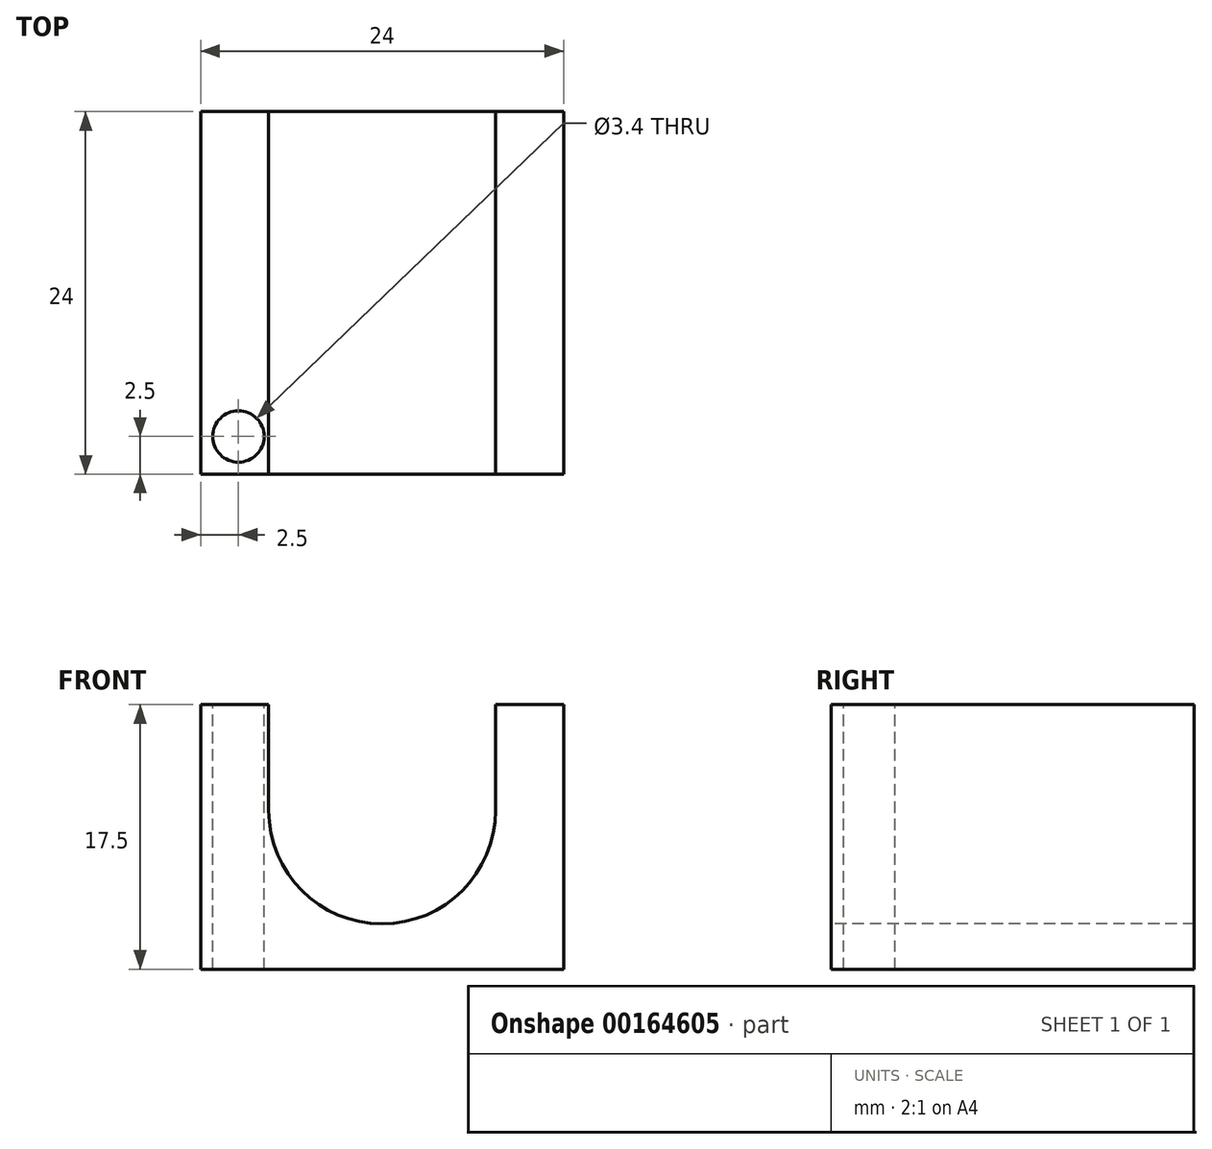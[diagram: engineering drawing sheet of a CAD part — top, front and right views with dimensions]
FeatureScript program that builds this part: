
annotation { "Feature Type Name" : "Feature", "Feature Type Description" : "" }
export const myFeature = defineFeature(function(context is Context, id is Id, definition is map)
    precondition{}
    {
        {
            var Q0;
            Q0=qCreatedBy(makeId("Top.planeOp"),FACE);
            var sketch = newSketch(context, id + "F0", { "sketchPlane" : qUnion([Q0])});
            skLineSegment(sketch, "E0.bottom", {"start": v(12, 12) * mm, "end": v(-12, 12) * mm});
            skLineSegment(sketch, "E0.top", {"start": v(12, -12) * mm, "end": v(-12, -12) * mm});
            skLineSegment(sketch, "E0.left", {"start": v(12, 12) * mm, "end": v(12, -12) * mm});
            skLineSegment(sketch, "E0.right", {"start": v(-12, 12) * mm, "end": v(-12, -12) * mm});
            skPoint(sketch, "E0.middle", {"position": v(0, 0) * mm});
            skSolve(sketch);
        }
        {
            var Q0;
            Q0=makeQuery(id+"F0.imprint","IMPRINT",FACE,{"disambiguationData":[TD([[makeQuery(id+"F0.imprint","IMPRINT",EDGE,{"derivedFrom":sQuery(id+"F0.wireOp",EDGE,"E0.bottom")}),1.0]])]});
            extrude(context, id + "F1", {"entities" : qUnion([Q0]), "depth" : 17.5 * mm});
        }
        {
            var Q0;
            Q0=makeQuery(id+"F1.opExtrude","SWEPT_FACE",FACE,{"disambiguationData":[OSD([sQuery(id+"F0.wireOp",EDGE,"E0.top")])]});
            var sketch = newSketch(context, id + "F2", { "sketchPlane" : qUnion([Q0])});
            skLineSegment(sketch, "E1.bottom", {"start": v(7.5, 17.5) * mm, "end": v(-7.5, 17.5) * mm});
            skLineSegment(sketch, "E1.top", {"start": v(7.5, 10.5) * mm, "end": v(-7.5, 10.5) * mm});
            skLineSegment(sketch, "E1.left", {"start": v(7.5, 17.5) * mm, "end": v(7.5, 10.5) * mm});
            skLineSegment(sketch, "E1.right", {"start": v(-7.5, 17.5) * mm, "end": v(-7.5, 10.5) * mm});
            skPoint(sketch, "E1.middle", {"position": v(0, 14) * mm});
            skCircle(sketch, "E2", {"center": v(0, 10.5) * mm, "radius": 7.5 * mm});
            skSolve(sketch);
        }
        {
            var Q0;
            {var subQ0=sQuery(id+"F2.wireOp",EDGE,"E1.top");Q0=makeQuery(id+"F2.imprint","IMPRINT",FACE,{"disambiguationData":[TD([[makeQuery(id+"F2.imprint","IMPRINT",EDGE,{"derivedFrom":subQ0}),1.0]])]});}
            var Q1;
            {var subQ4=sQuery(id+"F2.wireOp",EDGE,"E1.top");Q1=makeQuery(id+"F2.imprint","IMPRINT",FACE,{"disambiguationData":[TD([[makeQuery(id+"F2.imprint","IMPRINT",EDGE,{"derivedFrom":subQ4}),-1.0]])]});}
            var Q2;
            {var subQ0=sQuery(id+"F2.wireOp",EDGE,"E1.left");Q2=makeQuery(id+"F2.imprint","IMPRINT",FACE,{"disambiguationData":[TD([[makeQuery(id+"F2.imprint","IMPRINT",EDGE,{"derivedFrom":subQ0}),-1.0]])]});}
            var Q3;
            {var subQ0=sQuery(id+"F2.wireOp",EDGE,"E1.right");Q3=makeQuery(id+"F2.imprint","IMPRINT",FACE,{"disambiguationData":[TD([[makeQuery(id+"F2.imprint","IMPRINT",EDGE,{"derivedFrom":subQ0}),1.0]])]});}
            extrude(context, id + "F3", {"entities" : qUnion([Q0, Q1, Q2, Q3]), "operationType" : NewBodyOperationType.REMOVE, "oppositeDirection" : true, "depth" : 25 * mm});
        }
        {
            var Q0;
            {var subQ0=sQuery(id+"F0.wireOp",EDGE,"E0.bottom");var subQ1=sQuery(id+"F0.wireOp",EDGE,"E0.top");var subQ2=sQuery(id+"F0.wireOp",EDGE,"E0.right");Q0=makeQuery(id+"F3.boolean.opBoolean","SPLIT",FACE,{"disambiguationData":[TD([makeQuery(id+"F1.opExtrude","SWEPT_FACE",FACE,{"disambiguationData":[OSD([subQ2])]})])],"derivedFrom":makeQuery(id+"F1.opExtrude","CAP_FACE",FACE,{"disambiguationData":[OSD([subQ0,subQ1,sQuery(id+"F0.wireOp",EDGE,"E0.left"),subQ2])],"isStart":false})});}
            var sketch = newSketch(context, id + "F4", { "sketchPlane" : qUnion([Q0])});
            skPoint(sketch, "E3", {"position": v(-9.5, -9.5) * mm});
            skSolve(sketch);
        }
        {
            var Q0;
            Q0=sQuery(id+"F4.wireOp",VERTEX,"E3");
            var Q1;
            Q1=makeQuery(id+"F1.opExtrude","SWEPT_BODY",BODY,{"disambiguationData":[OSD([sQuery(id+"F0.wireOp",EDGE,"E0.bottom"),sQuery(id+"F0.wireOp",EDGE,"E0.top"),sQuery(id+"F0.wireOp",EDGE,"E0.left"),sQuery(id+"F0.wireOp",EDGE,"E0.right")])]});
            hole(context, id + "F5", {"style" : HoleStyle.SIMPLE, "endStyle" : HoleEndStyle.THROUGH, "holeDiameter" : 3.4 * mm, "locations" : qUnion([Q0]), "scope" : qUnion([Q1]), "isTappedThrough" : true});
        }
        {
            var Q0;
            Q0=qCreatedBy(makeId("Right.planeOp"),FACE);
            var sketch = newSketch(context, id + "F6", { "sketchPlane" : qUnion([Q0])});
            skLineSegment(sketch, "E4", {"start": v(0, 0) * mm, "end": v(0, 30.28) * mm, "construction": true});
            skSolve(sketch);
        }
    });
